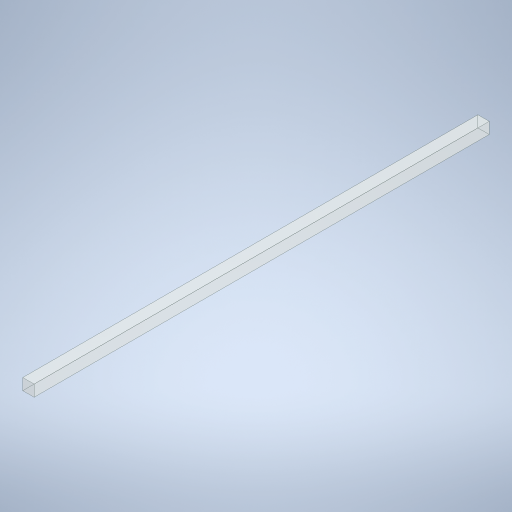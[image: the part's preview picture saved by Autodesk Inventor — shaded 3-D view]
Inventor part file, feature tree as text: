
AUTODESK INVENTOR PART (.ipt)
format: ipt  version: 2024 (Build 280153000, 153)  size: 260,096 bytes
history: native  units: in
note: dims shown in document units (in); Inventor stores cm internally (conversion verified against a paired STEP export)
features: extrude x1, sketch x1
ambient origin geometry x8: Origin, YZ Plane, XZ Plane, XY Plane, X Axis, Y Axis, Z Axis, Center Point
bodies: Solid1 (feature_tree)
feature tree (2):
  extrude  "Extrusion1"  Depth=7.5in
  sketch  "Sketch1"  dims[d0=300.0in d1=7.5in d2=7.5in d3=0.0in]
